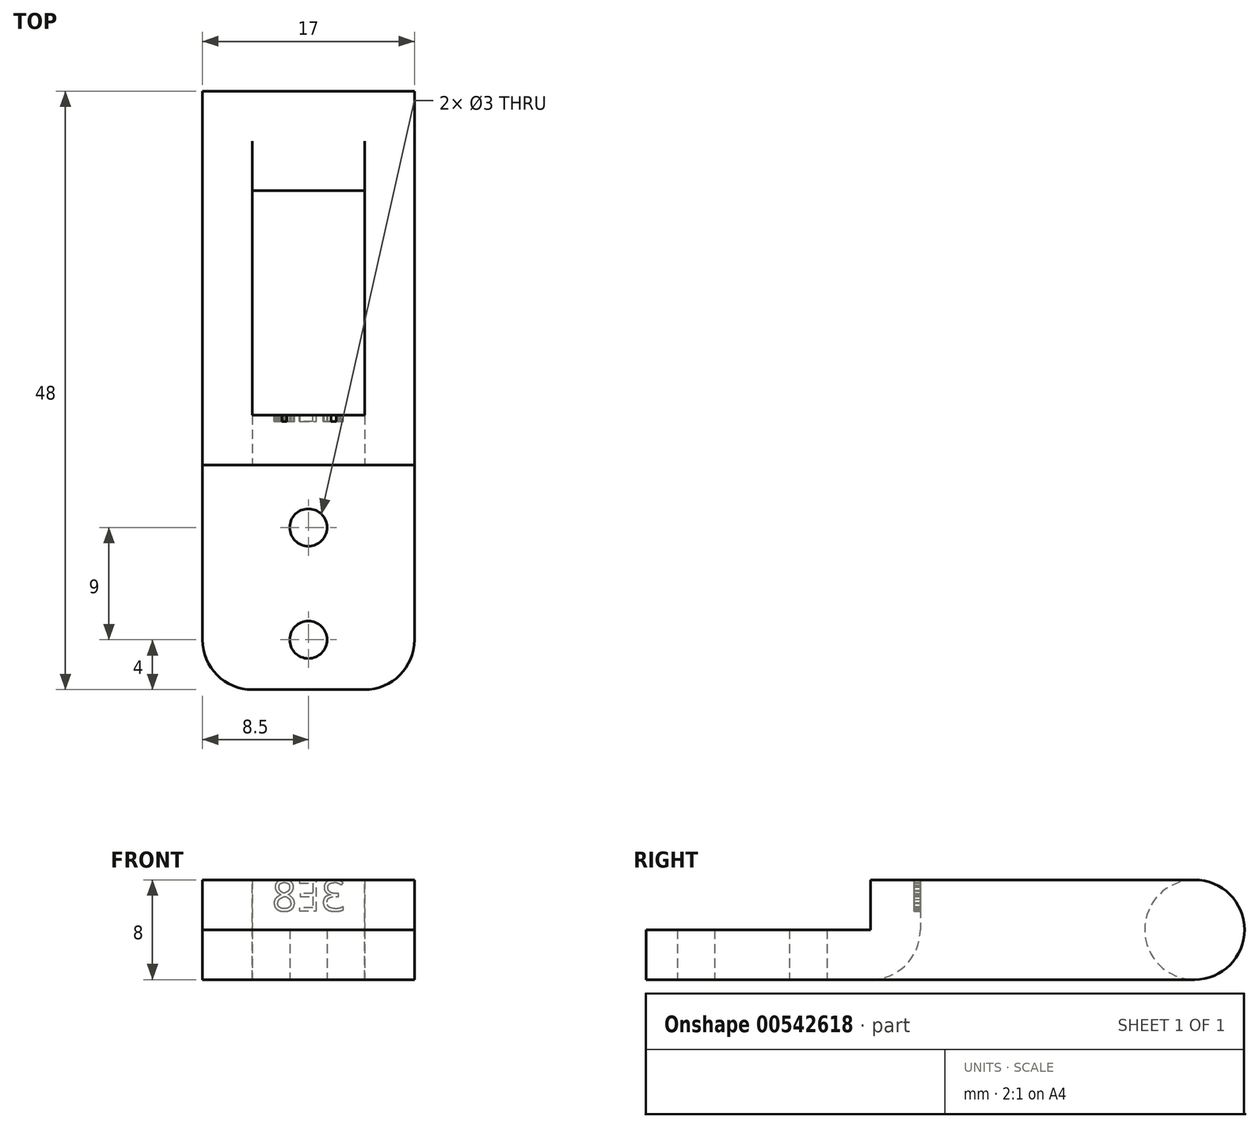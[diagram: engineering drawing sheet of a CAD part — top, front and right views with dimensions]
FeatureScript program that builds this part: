
annotation { "Feature Type Name" : "Feature", "Feature Type Description" : "" }
export const myFeature = defineFeature(function(context is Context, id is Id, definition is map)
    precondition{}
    {
        {
            assignVariable(context, id + "F0", {"name" : "hingethick", "anyValue" : 4});
        }
        {
            assignVariable(context, id + "F1", {"name" : "panelthick", "anyValue" : 4});
        }
        {
            var Q0;
            Q0=qCreatedBy(makeId("Top.planeOp"),FACE);
            var sketch = newSketch(context, id + "F2", { "sketchPlane" : qUnion([Q0])});
            skLineSegment(sketch, "E0.bottom", {"start": v(8.5, -24) * mm, "end": v(-8.5, -24) * mm});
            skLineSegment(sketch, "E0.top", {"start": v(8.5, 24) * mm, "end": v(-8.5, 24) * mm});
            skLineSegment(sketch, "E0.left", {"start": v(8.5, -24) * mm, "end": v(8.5, 24) * mm});
            skLineSegment(sketch, "E0.right", {"start": v(-8.5, -24) * mm, "end": v(-8.5, 24) * mm});
            skPoint(sketch, "E0.middle", {"position": v(0, 0) * mm});
            skLineSegment(sketch, "E1.bottom", {"start": v(4.5, -2) * mm, "end": v(-4.5, -2) * mm});
            skLineSegment(sketch, "E1.top", {"start": v(4.5, 16) * mm, "end": v(-4.5, 16) * mm});
            skLineSegment(sketch, "E1.left", {"start": v(4.5, -2) * mm, "end": v(4.5, 16) * mm});
            skLineSegment(sketch, "E1.right", {"start": v(-4.5, -2) * mm, "end": v(-4.5, 16) * mm});
            skPoint(sketch, "E1.middle", {"position": v(0, 7) * mm});
            skCircle(sketch, "E2", {"center": v(0, -11) * mm, "radius": 1.5 * mm});
            skLineSegment(sketch, "E3", {"start": v(0, 16) * mm, "end": v(0, 24) * mm, "construction": true});
            skLineSegment(sketch, "E4", {"start": v(0, -2) * mm, "end": v(0, -11) * mm, "construction": true});
            skLineSegment(sketch, "E5", {"start": v(0, -11) * mm, "end": v(0, -20) * mm, "construction": true});
            skLineSegment(sketch, "E6", {"start": v(4.5, 7) * mm, "end": v(8.5, 7) * mm, "construction": true});
            skCircle(sketch, "E7", {"center": v(0, -20) * mm, "radius": 1.5 * mm});
            skLineSegment(sketch, "E8", {"start": v(0, -20) * mm, "end": v(0, -24) * mm, "construction": true});
            skSolve(sketch);
        }
        {
            var Q0;
            Q0 = qSketchRegion(id + "F2", true);
            extrude(context, id + "F3", {"entities" : qUnion([Q0]), "depth" : (getVariable(context, 'hingethick')) * mm, "offsetDistance" : 25 * mm});
        }
        {
            var Q0;
            Q0=makeQuery(id+"F3.opExtrude","CAP_FACE",FACE,{"disambiguationData":[OSD([sQuery(id+"F2.wireOp",EDGE,"E0.bottom"),sQuery(id+"F2.wireOp",EDGE,"E0.top"),sQuery(id+"F2.wireOp",EDGE,"E0.left"),sQuery(id+"F2.wireOp",EDGE,"E0.right"),sQuery(id+"F2.wireOp",EDGE,"E1.bottom"),sQuery(id+"F2.wireOp",EDGE,"E1.top"),sQuery(id+"F2.wireOp",EDGE,"E1.left"),sQuery(id+"F2.wireOp",EDGE,"E1.right"),sQuery(id+"F2.wireOp",EDGE,"E2")])],"isStart":false});
            var sketch = newSketch(context, id + "F4", { "sketchPlane" : qUnion([Q0])});
            skLineSegment(sketch, "E9.0", {"start": v(-4.5, -2) * mm, "end": v(-4.5, 16) * mm});
            skLineSegment(sketch, "E10.0", {"start": v(4.5, -2) * mm, "end": v(-4.5, -2) * mm});
            skLineSegment(sketch, "E11.0", {"start": v(4.5, 16) * mm, "end": v(-4.5, 16) * mm});
            skLineSegment(sketch, "E12.0", {"start": v(4.5, -2) * mm, "end": v(4.5, 16) * mm});
            skLineSegment(sketch, "E13.0", {"start": v(8.5, -24) * mm, "end": v(8.5, 24) * mm});
            skLineSegment(sketch, "E14.0", {"start": v(8.5, 24) * mm, "end": v(-8.5, 24) * mm});
            skLineSegment(sketch, "E15.0", {"start": v(-8.5, -24) * mm, "end": v(-8.5, 24) * mm});
            skLineSegment(sketch, "E16.0", {"start": v(0, 16) * mm, "end": v(0, 24) * mm, "construction": true});
            skLineSegment(sketch, "E17", {"start": v(-8.5, -6) * mm, "end": v(8.5, -6) * mm});
            skLineSegment(sketch, "E18", {"start": v(0, -2) * mm, "end": v(0, -6) * mm, "construction": true});
            skSolve(sketch);
        }
        {
            var Q0;
            Q0 = qSketchRegion(id + "F4", true);
            extrude(context, id + "F5", {"entities" : qUnion([Q0]), "operationType" : NewBodyOperationType.ADD, "depth" : (getVariable(context, 'panelthick')) * mm, "offsetDistance" : 25 * mm});
        }
        {
            var Q0;
            Q0=makeQuery(id+"F5.opExtrude","CAP_EDGE",EDGE,{"disambiguationData":[OSD([sQuery(id+"F4.wireOp",EDGE,"E11.0")])],"isStart":false});
            var Q1;
            Q1=makeQuery(id+"F3.opExtrude","CAP_EDGE",EDGE,{"disambiguationData":[OSD([sQuery(id+"F2.wireOp",EDGE,"E1.top")])],"isStart":true});
            var Q2;
            Q2=makeQuery(id+"F3.opExtrude","CAP_EDGE",EDGE,{"disambiguationData":[OSD([sQuery(id+"F2.wireOp",EDGE,"E0.top")])],"isStart":true});
            var Q3;
            Q3=makeQuery(id+"F5.opExtrude","CAP_EDGE",EDGE,{"disambiguationData":[OSD([sQuery(id+"F4.wireOp",EDGE,"E14.0")])],"isStart":false});
            var Q4;
            Q4=makeQuery(id+"F3.opExtrude","SWEPT_EDGE",EDGE,{"disambiguationData":[OSD([sQuery(id+"F2.wireOp",EDGE,"E0.bottom"),sQuery(id+"F2.wireOp",EDGE,"E0.right")])]});
            var Q5;
            Q5=makeQuery(id+"F3.opExtrude","SWEPT_EDGE",EDGE,{"disambiguationData":[OSD([sQuery(id+"F2.wireOp",EDGE,"E0.bottom"),sQuery(id+"F2.wireOp",EDGE,"E0.left")])]});
            var Q6;
            Q6=makeQuery(id+"F3.opExtrude","CAP_EDGE",EDGE,{"disambiguationData":[OSD([sQuery(id+"F2.wireOp",EDGE,"E1.bottom")])],"isStart":true});
            fillet(context, id + "F6", {"entities" : qUnion([Q0, Q1, Q2, Q3, Q4, Q5, Q6]), "radius" : ((getVariable(context, 'hingethick') + getVariable(context, 'panelthick')) / 2) * mm, "tangentPropagation" : true, "allowEdgeOverflow" : false});
        }
        {
            var Q0;
            Q0=makeQuery(id+"F5.boolean.opBoolean","MERGE",FACE,{"derivedFrom":[makeQuery(id+"F3.opExtrude","SWEPT_FACE",FACE,{"disambiguationData":[OSD([sQuery(id+"F2.wireOp",EDGE,"E1.bottom")])]}),makeQuery(id+"F5.opExtrude","SWEPT_FACE",FACE,{"disambiguationData":[OSD([sQuery(id+"F4.wireOp",EDGE,"E10.0")])]})]});
            var sketch = newSketch(context, id + "F7", { "sketchPlane" : qUnion([Q0])});
            skText(sketch, "E19", { "text": "3E8", "fontName": "OpenSans-Regular.ttf"});
            skLineSegment(sketch, "E20", {"start": v(4.5, 4) * mm, "end": v(-4.5, 8) * mm, "construction": true});
            skPoint(sketch, "E21", {"position": v(0, 6) * mm});
            const initialGuessF7  = {"E19": [-0.00297, 0.0055, 1, 0, 0.0025]};
            skSetInitialGuess(sketch, initialGuessF7);
            skSolve(sketch);
        }
        {
            var Q0;
            Q0 = qSketchRegion(id + "F7", true);
            extrude(context, id + "F8", {"entities" : qUnion([Q0]), "operationType" : NewBodyOperationType.REMOVE, "oppositeDirection" : true, "depth" : .5 * mm, "offsetDistance" : 25 * mm});
        }
    });
